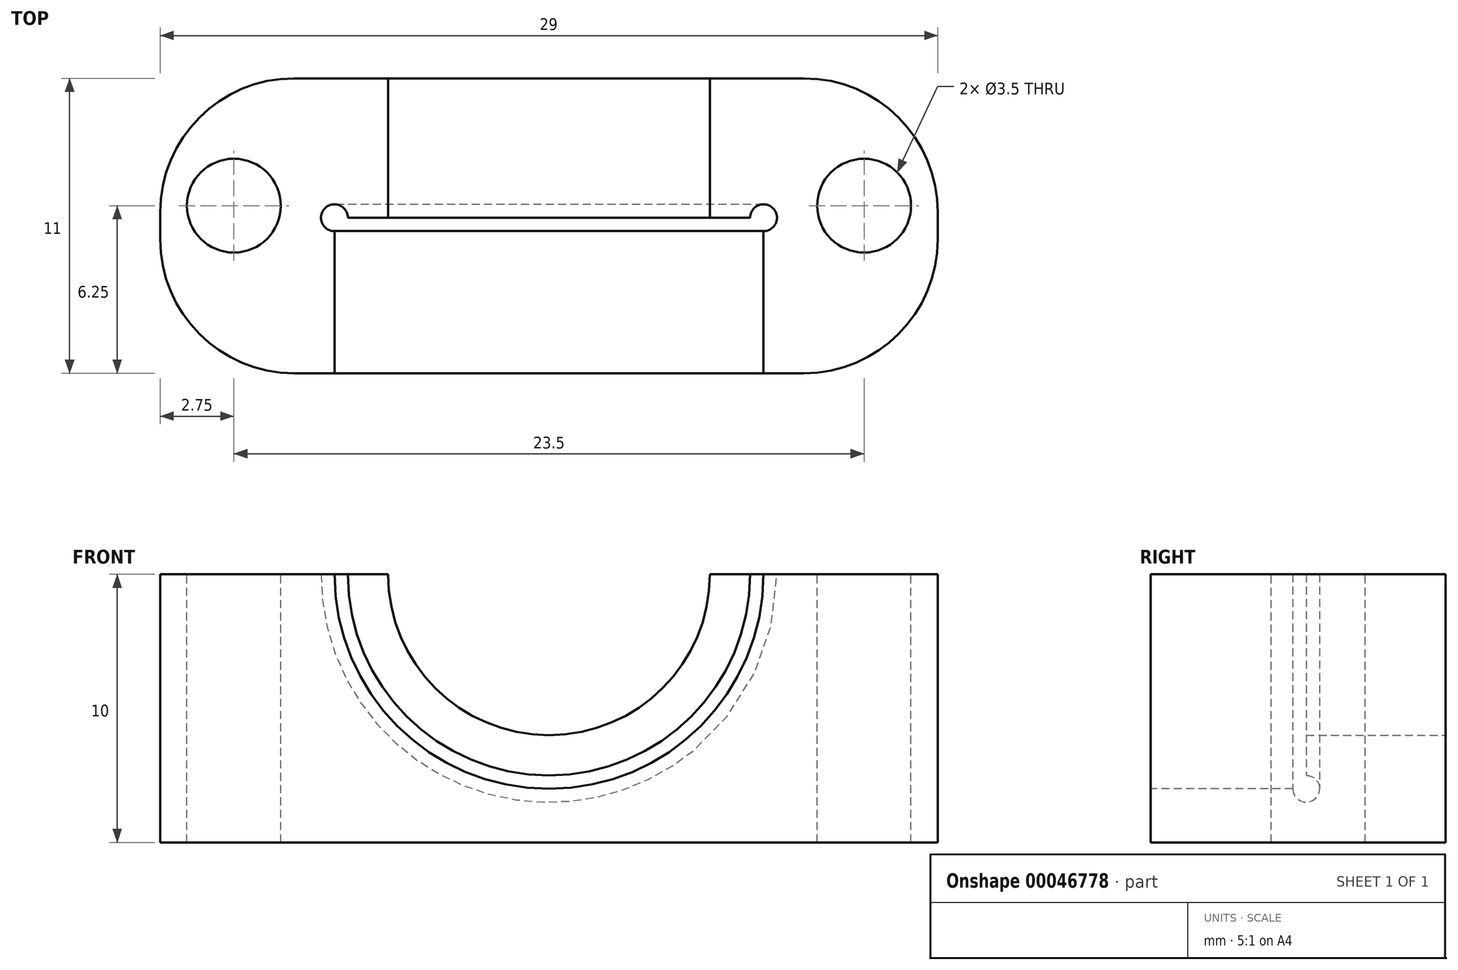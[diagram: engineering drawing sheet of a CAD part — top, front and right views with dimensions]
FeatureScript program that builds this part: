
annotation { "Feature Type Name" : "Feature", "Feature Type Description" : "" }
export const myFeature = defineFeature(function(context is Context, id is Id, definition is map)
    precondition{}
    {
        {
            var Q0;
            Q0=qCreatedBy(makeId("Top.planeOp"),FACE);
            var sketch = newSketch(context, id + "F0", { "sketchPlane" : qUnion([Q0])});
            skLineSegment(sketch, "E0.bottom", {"start": v(0, 0) * mm, "end": v(25, 0) * mm});
            skLineSegment(sketch, "E0.top", {"start": v(0, 11) * mm, "end": v(25, 11) * mm});
            skLineSegment(sketch, "E0.left", {"start": v(0, 0) * mm, "end": v(0, 11) * mm});
            skLineSegment(sketch, "E0.right", {"start": v(25, 0) * mm, "end": v(25, 11) * mm});
            skSolve(sketch);
        }
        {
            var Q0;
            Q0=qSketchRegion(id+"F0",true);
            extrude(context, id + "F1", {"entities" : qUnion([Q0]), "depth" : 10 * mm});
        }
        {
            var Q0;
            Q0=makeQuery(id+"F1.opExtrude","SWEPT_FACE",FACE,{"disambiguationData":[OSD([sQuery(id+"F0.wireOp",EDGE,"E0.bottom")])]});
            var sketch = newSketch(context, id + "F2", { "sketchPlane" : qUnion([Q0])});
            skCircle(sketch, "E1", {"center": v(12.5, 10) * mm, "radius": 8 * mm});
            skSolve(sketch);
        }
        {
            var Q0;
            Q0=qSketchRegion(id+"F2",true);
            extrude(context, id + "F3", {"entities" : qUnion([Q0]), "operationType" : NewBodyOperationType.REMOVE, "oppositeDirection" : true, "depth" : 5.8 * mm});
        }
        {
            var Q0;
            Q0=makeQuery(id+"F1.opExtrude","SWEPT_FACE",FACE,{"disambiguationData":[OSD([sQuery(id+"F0.wireOp",EDGE,"E0.top")])]});
            var sketch = newSketch(context, id + "F4", { "sketchPlane" : qUnion([Q0])});
            skCircle(sketch, "E2", {"center": v(-12.5, 10) * mm, "radius": 6 * mm});
            skSolve(sketch);
        }
        {
            var Q0;
            Q0=qSketchRegion(id+"F4",true);
            extrude(context, id + "F5", {"entities" : qUnion([Q0]), "operationType" : NewBodyOperationType.REMOVE, "oppositeDirection" : true, "depth" : 6 * mm});
        }
        {
            var Q0;
            Q0=makeQuery(id+"F1.opExtrude","SWEPT_FACE",FACE,{"disambiguationData":[OSD([sQuery(id+"F0.wireOp",EDGE,"E0.left")])]});
            var sketch = newSketch(context, id + "F6", { "sketchPlane" : qUnion([Q0])});
            skLineSegment(sketch, "E3.bottom", {"start": v(-11, 0) * mm, "end": v(0, 0) * mm});
            skLineSegment(sketch, "E3.top", {"start": v(-11, 10) * mm, "end": v(0, 10) * mm});
            skLineSegment(sketch, "E3.left", {"start": v(-11, 0) * mm, "end": v(-11, 10) * mm});
            skLineSegment(sketch, "E3.right", {"start": v(0, 0) * mm, "end": v(0, 10) * mm});
            skSolve(sketch);
        }
        {
            var Q0;
            Q0=qSketchRegion(id+"F6",true);
            extrude(context, id + "F7", {"entities" : qUnion([Q0]), "operationType" : NewBodyOperationType.ADD, "depth" : 2 * mm});
        }
        {
            var Q0;
            Q0=makeQuery(id+"F1.opExtrude","SWEPT_FACE",FACE,{"disambiguationData":[OSD([sQuery(id+"F0.wireOp",EDGE,"E0.right")])]});
            var sketch = newSketch(context, id + "F8", { "sketchPlane" : qUnion([Q0])});
            skLineSegment(sketch, "E4.bottom", {"start": v(11, 10) * mm, "end": v(0, 10) * mm});
            skLineSegment(sketch, "E4.top", {"start": v(11, 0) * mm, "end": v(0, 0) * mm});
            skLineSegment(sketch, "E4.left", {"start": v(11, 10) * mm, "end": v(11, 0) * mm});
            skLineSegment(sketch, "E4.right", {"start": v(0, 10) * mm, "end": v(0, 0) * mm});
            skSolve(sketch);
        }
        {
            var Q0;
            Q0=qSketchRegion(id+"F8",true);
            extrude(context, id + "F9", {"entities" : qUnion([Q0]), "operationType" : NewBodyOperationType.ADD, "depth" : 2 * mm});
        }
        {
            var Q0;
            Q0=makeQuery(id+"F9.opExtrude","CAP_EDGE",EDGE,{"disambiguationData":[OSD([sQuery(id+"F8.wireOp",EDGE,"E4.left")])],"isStart":false});
            var Q1;
            Q1=makeQuery(id+"F9.opExtrude","CAP_EDGE",EDGE,{"disambiguationData":[OSD([sQuery(id+"F8.wireOp",EDGE,"E4.right")])],"isStart":false});
            var Q2;
            Q2=makeQuery(id+"F7.opExtrude","CAP_EDGE",EDGE,{"disambiguationData":[OSD([sQuery(id+"F6.wireOp",EDGE,"E3.left")])],"isStart":false});
            var Q3;
            Q3=makeQuery(id+"F7.opExtrude","CAP_EDGE",EDGE,{"disambiguationData":[OSD([sQuery(id+"F6.wireOp",EDGE,"E3.right")])],"isStart":false});
            fillet(context, id + "F10", {"entities" : qUnion([Q0, Q1, Q2, Q3]), "radius" : 5 * mm, "tangentPropagation" : true, "allowEdgeOverflow" : false});
        }
        {
            var Q0;
            {var subQ0=sQuery(id+"F0.wireOp",EDGE,"E0.bottom");var subQ1=sQuery(id+"F0.wireOp",EDGE,"E0.top");var subQ2=sQuery(id+"F0.wireOp",EDGE,"E0.left");Q0=makeQuery(id+"F5.boolean.opBoolean","SPLIT",FACE,{"disambiguationData":[TD([makeQuery(id+"F1.opExtrude","SWEPT_FACE",FACE,{"disambiguationData":[OSD([subQ2])]})])],"derivedFrom":makeQuery(id+"F1.opExtrude","CAP_FACE",FACE,{"disambiguationData":[OSD([subQ0,subQ1,subQ2,sQuery(id+"F0.wireOp",EDGE,"E0.right")])],"isStart":false})});}
            var sketch = newSketch(context, id + "F11", { "sketchPlane" : qUnion([Q0])});
            skCircle(sketch, "E5", {"center": v(0.75, 6.25) * mm, "radius": 1.75 * mm});
            skCircle(sketch, "E6", {"center": v(24.25, 6.25) * mm, "radius": 1.75 * mm});
            skSolve(sketch);
        }
        {
            var Q0;
            Q0=qSketchRegion(id+"F11",true);
            extrude(context, id + "F12", {"entities" : qUnion([Q0]), "operationType" : NewBodyOperationType.REMOVE, "oppositeDirection" : true, "depth" : 25 * mm});
        }
        {
            var Q0;
            {var subQ0=sQuery(id+"F0.wireOp",EDGE,"E0.bottom");var subQ1=sQuery(id+"F0.wireOp",EDGE,"E0.top");var subQ2=sQuery(id+"F0.wireOp",EDGE,"E0.right");Q0=makeQuery(id+"F9.boolean.opBoolean","MERGE",FACE,{"derivedFrom":[makeQuery(id+"F5.boolean.opBoolean","SPLIT",FACE,{"disambiguationData":[TD([makeQuery(id+"F1.opExtrude","SWEPT_FACE",FACE,{"disambiguationData":[OSD([subQ2])]})])],"derivedFrom":makeQuery(id+"F1.opExtrude","CAP_FACE",FACE,{"disambiguationData":[OSD([subQ0,subQ1,sQuery(id+"F0.wireOp",EDGE,"E0.left"),subQ2])],"isStart":false})}),makeQuery(id+"F9.opExtrude","SWEPT_FACE",FACE,{"disambiguationData":[OSD([sQuery(id+"F8.wireOp",EDGE,"E4.bottom")])]})]});}
            var sketch = newSketch(context, id + "F13", { "sketchPlane" : qUnion([Q0])});
            skCircle(sketch, "E7", {"center": v(20.5, 5.8) * mm, "radius": 0.5 * mm});
            skSolve(sketch);
        }
        {
            var Q0;
            {var subQ0=makeQuery(id+"F1.opExtrude","CAP_FACE",FACE,{"disambiguationData":[OSD([sQuery(id+"F0.wireOp",EDGE,"E0.bottom"),sQuery(id+"F0.wireOp",EDGE,"E0.top"),sQuery(id+"F0.wireOp",EDGE,"E0.left"),sQuery(id+"F0.wireOp",EDGE,"E0.right")])],"isStart":false});var subQ1=sQuery(id+"F2.wireOp",EDGE,"E1");var subQ2=makeQuery(id+"F3.boolean.opBoolean","INTERSECT",EDGE,{"disambiguationData":[OD(1.0)],"derivedFrom":[subQ0,makeQuery(id+"F3.opExtrude","SWEPT_FACE",FACE,{"disambiguationData":[OSD([subQ1])]})]});var subQ3=sQuery(id+"F13.wireOp",EDGE,"E7");var subQ4=makeQuery(id+"F13.imprint","INTERSECT",VERTEX,{"derivedFrom":[subQ2,subQ3]});Q0=makeQuery(id+"F13.imprint","IMPRINT",FACE,{"disambiguationData":[TD([[makeQuery(id+"F13.imprint","IMPRINT",EDGE,{"disambiguationData":[TD([[subQ4,-1.0]])],"derivedFrom":subQ3}),1.0]])]});}
            var Q1;
            Q1=makeQuery(id+"F5.boolean.opBoolean","COPY",FACE,{"derivedFrom":makeQuery(id+"F5.opExtrude","SWEPT_FACE",FACE,{"disambiguationData":[OSD([sQuery(id+"F4.wireOp",EDGE,"E2")])]})});
            revolve(context, id + "F14", {"operationType" : NewBodyOperationType.REMOVE, "entities" : qUnion([Q0]), "axis" : qUnion([Q1]), "revolveType" : RevolveType.FULL, "oppositeDirection" : true});
        }
    });
